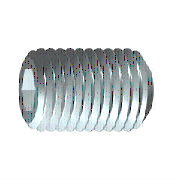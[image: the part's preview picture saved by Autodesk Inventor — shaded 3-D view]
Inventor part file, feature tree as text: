
AUTODESK INVENTOR PART (.ipt)
format: ipt  version: 2020 (Build 240168000, 168)  size: 175,104 bytes
history: native  units: mm (DEFAULTED — no unit token found)
features: sketch x2, extrude x1, other x1, plane x1
ambient origin geometry x8: Origin, YZ Plane, XZ Plane, XY Plane, X Axis, Y Axis, Z Axis, Center Point
bodies: Solid1 (feature_tree), Body (feature_tree)
feature tree (5):
  extrude  "Slot"  TaperAngle=60.0deg  [1 undecoded]
  other  "Work Axis1"
  plane  "Work Plane1"
  sketch  "Sketch1"  dims[d0=2.032mm d1=60.0deg]
  sketch  "Sketch2"  dims[d2=4.1656mm d3=2.287693mm d6=90.0deg d4=4.7625mm d5=10.297443mm d7=2.0828mm d8=2.032mm d9=0.0mm d10=1.0414mm d11=45.0deg d12=0.42926mm d13=45.0deg d14=4.7625mm d15=0.0mm d16=0.0mm d33=1.0414mm d34=0.42926mm d35=0.0mm d37=0.0mm]
note: 1 required parameter value undecoded (feature->parameter linkage not recoverable at this tier; creation-order binding heuristic only, values carry confidence <= 0.55)
